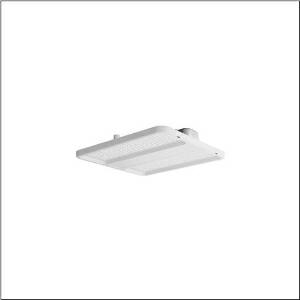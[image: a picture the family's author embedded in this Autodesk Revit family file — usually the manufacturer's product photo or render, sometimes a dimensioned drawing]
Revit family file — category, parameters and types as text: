
# Revit family: highbay_11_midi_51hn11da4hda
name_source: partatom
category: Lighting Fixtures
units: mm (PartAtom-declared; Revit-internal decimal feet)

## family parameters
Cut with Voids When Loaded = No
Host = Face
Light Source = No
Part Type = Normal
Room Calculation Point = No
Round Connector Dimension = Use Diameter
Shared = No

## types (1)
- --- (1 x LED, 2890 lm, 14.5 W, 4000K)
    Apparent Load = 15 VA
    CIE Flux Codes = 85 97 100 100 100
    Color Rendering = 80
    Color Temperature = 4000K
    Default Elevation = 1800 mm
    Description = high bay luminaire Highbay 11 midi; direct symmetric narrow distribution, light control with lens of PMMA; UGR ≤ 22 (X = 4H | Y = 8H | S = 0.25H | reflection values 70/50/20); luminous flux: 18.500lm; light colour: 840, colour temperature: 4000K, MacAdam ≤ 2 SDCM (initial), colour rendering: CRI > 80; luminous efficacy: 201,5lm/W; rated service life: 100.000h (L95/B50) at AT= 25°C; control: DALI 2; housing frame of high-performance plastic PA6, matt traffic white (RAL 9016); cover of PMMA; dimension (LxWxH): 474 x 442 x 72mm; luminaire connection: terminal, 5-pole, max. 2.5mm² (cable entry for one cable, Ø 8.5..16mm); mains connection: 230..240V, AC/DC 0/50..60Hz; connected load: 91,8W; protection rating (complete): IP66; insulation class (complete): insulation class I (protective earthing); protection symbol: D; impact resistance: IK08; halogen-free wiring; for central battery installations according to DIN EN 60598-2-22; corresponds to IFS (International Featured Standards) requirements for safety and quality in the food industry; LABS conformity tested according to VDMA 24364:2018-05; certification: CE, ENEC, VDE, UKCA; permissible operating ambient temperature: -40..+60°C (reducing of maximum allowable ambient temperature of 5°C with ceiling mounting); packaging unit: 1 piece; (delivery without accessories; please order mounting accessories separately)
    Height = 72 mm  [stored 0.23622 ft]
    Lamp = 1 x LED
    Lamp Light Flux = 2890 lm
    Lamp Power = 14.5 W
    Lamp count = 1
    Length = 474 mm
    Luminous efficacy = 199 lm/W
    Manufacturer = Siteco
    ModVariant = No
    Model = 51HN11DA4HDA
    Mounting Place = Ceiling
    Mounting Type = Pendant
    Number of Poles = 1
    OnlyDefault = Yes
    Power Factor = 1
    Product Name = Highbay 11 midi
    Product group = high bay luminaire
    ProductGroupID = 901
    Protection Class = Protection class I
    Protection Degree = IP 66
    RLX_Detail_Level = 1
    RLX_Emergency_Light_Flux = 0 lm
    RLX_Emergency_Type = 0
    RLX_Emergency_Type_DB = No
    RlxData = <blob elided: 16733 chars, md5=2bc52da8>
    Socket = socket
    Standby Power = 0 W
    System Light Flux = 2890 lm
    System Power = 15 W
    Type Comments = : DC mode (central or group accumulator) initial emergency light level
    Type Image = l_1363240.jpg
    URL = http://relux.com
    VarID = @adj_003725
    Voltage = 0 V
    Weight = 0.00 kg
    Width = 442 mm

note: [stored X ft] marks values corroborated as IEEE doubles in the binary element streams (Revit-internal decimal feet)

## geometry (parser evidence)
native form markers: Blend x4, Sweep x10
no freeform markers — native parametric forms only
